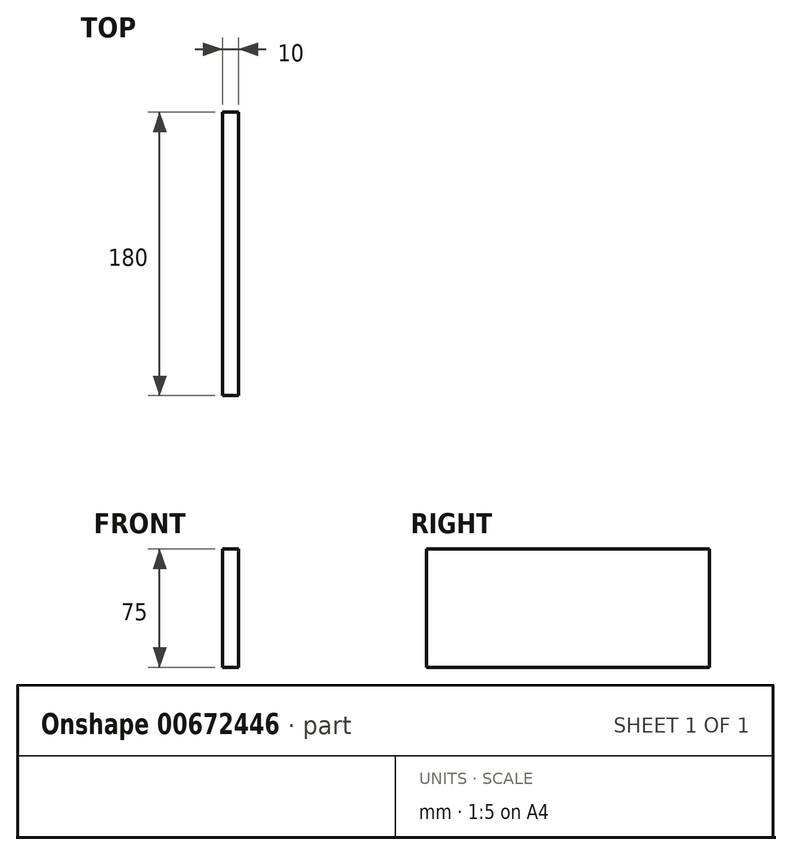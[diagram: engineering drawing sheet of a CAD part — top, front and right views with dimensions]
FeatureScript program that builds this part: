
annotation { "Feature Type Name" : "Feature", "Feature Type Description" : "" }
export const myFeature = defineFeature(function(context is Context, id is Id, definition is map)
    precondition{}
    {
        {
            var Q0;
            Q0=qCreatedBy(makeId("Right.planeOp"),FACE);
            var sketch = newSketch(context, id + "F0", { "sketchPlane" : qUnion([Q0])});
            skLineSegment(sketch, "E0.bottom", {"start": v(90, -37.5) * mm, "end": v(-90, -37.5) * mm});
            skLineSegment(sketch, "E0.top", {"start": v(90, 37.5) * mm, "end": v(-90, 37.5) * mm});
            skLineSegment(sketch, "E0.left", {"start": v(90, -37.5) * mm, "end": v(90, 37.5) * mm});
            skLineSegment(sketch, "E0.right", {"start": v(-90, -37.5) * mm, "end": v(-90, 37.5) * mm});
            skPoint(sketch, "E0.middle", {"position": v(0, 0) * mm});
            skSolve(sketch);
        }
        {
            var Q0;
            Q0 = qSketchRegion(id + "F0", true);
            extrude(context, id + "F1", {"entities" : qUnion([Q0]), "depth" : 10 * mm, "offsetDistance" : 25 * mm});
        }
    });
